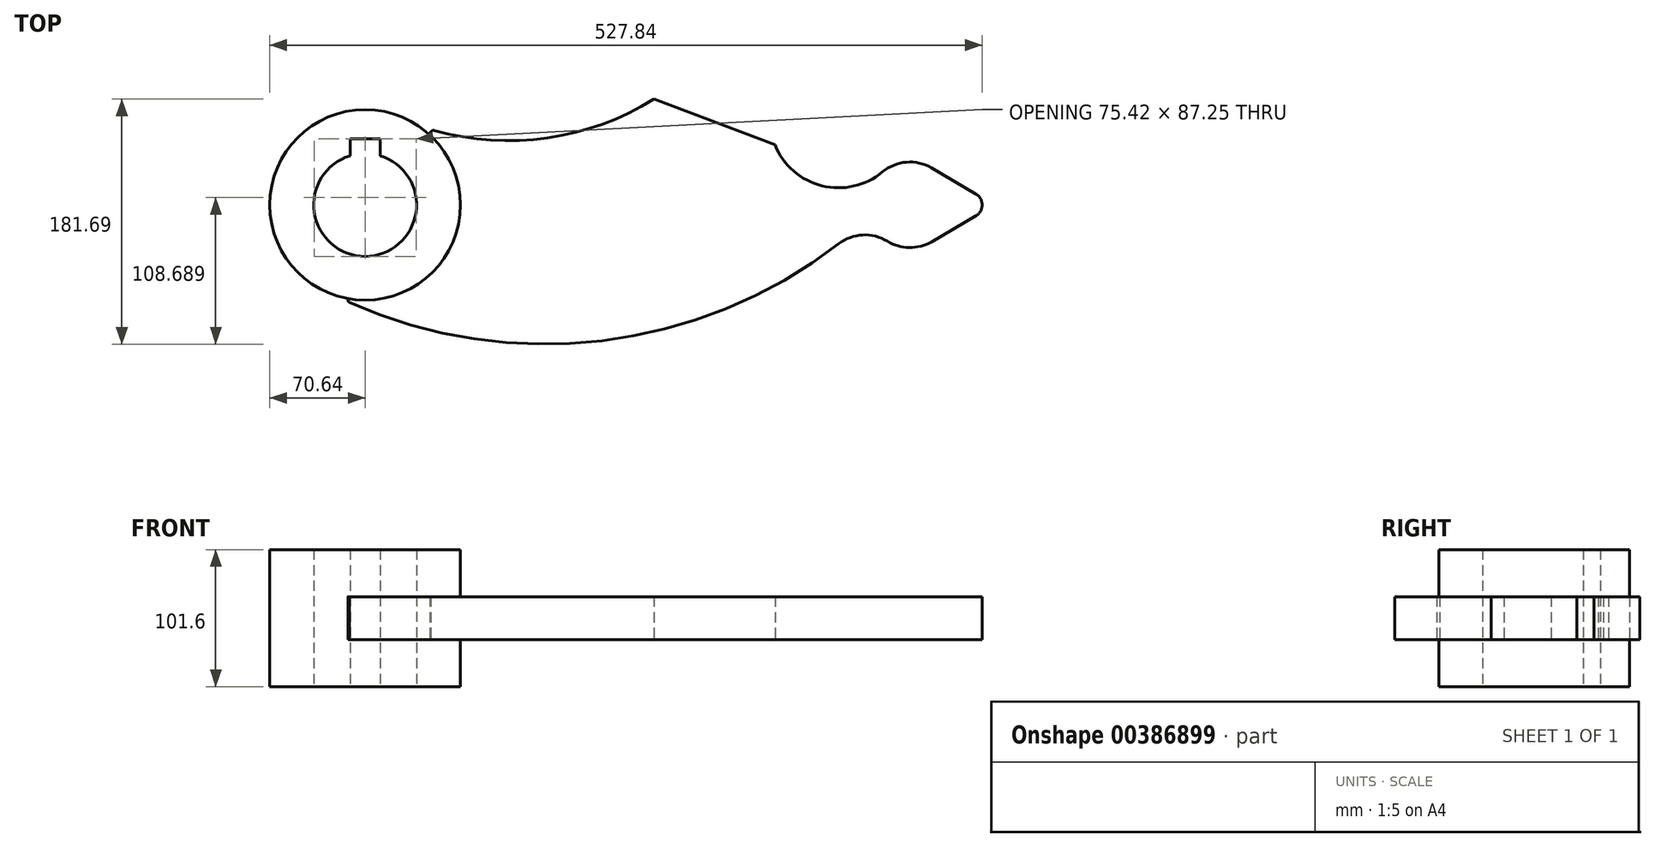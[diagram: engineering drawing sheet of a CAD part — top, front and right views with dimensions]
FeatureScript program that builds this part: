
annotation { "Feature Type Name" : "Feature", "Feature Type Description" : "" }
export const myFeature = defineFeature(function(context is Context, id is Id, definition is map)
    precondition{}
    {
        {
            var Q0;
            Q0=qCreatedBy(makeId("Top.planeOp"),FACE);
            var sketch = newSketch(context, id + "F0", { "sketchPlane" : qUnion([Q0])});
            skArc(sketch, "E0", {"start": v(51.32, 55.22) * mm, "mid": v(135.14, 49.67) * mm, "end": v(214.04, 78.5) * mm});
            skArc(sketch, "E1", {"start": v(303.74, 44.45) * mm, "mid": v(338.47, 14.23) * mm, "end": v(383.35, 24.47) * mm});
            skArc(sketch, "E2", {"start": v(452.47, -8.23) * mm, "mid": v(457.2, -0.02) * mm, "end": v(452.5, 8.21) * mm});
            skArc(sketch, "E3", {"start": v(387, -26.95) * mm, "mid": v(403.28, -31.67) * mm, "end": v(419.67, -27.35) * mm});
            skArc(sketch, "E4", {"start": v(387, -26.95) * mm, "mid": v(368.67, -22.27) * mm, "end": v(350.92, -28.86) * mm});
            skPoint(sketch, "E4.first.point", {"position": v(350.92, -28.86) * mm});
            skPoint(sketch, "E4.third.point", {"position": v(372.44, -85.66) * mm});
            skLineSegment(sketch, "E5", {"start": v(214.04, 78.5) * mm, "end": v(303.74, 44.45) * mm});
            skLineSegment(sketch, "E6", {"start": v(419.67, -27.35) * mm, "end": v(452.47, -8.23) * mm});
            skLineSegment(sketch, "E7", {"start": v(452.5, 8.21) * mm, "end": v(419.76, 27.45) * mm});
            skArc(sketch, "E8.trimOffspring", {"start": v(419.76, 27.45) * mm, "mid": v(401.08, 31.72) * mm, "end": v(383.35, 24.47) * mm});
            skArc(sketch, "E9", {"start": v(-11.14, -69.76) * mm, "mid": v(-12.63, -70.64) * mm, "end": v(-11.86, -72.19) * mm});
            skPoint(sketch, "E9.first.point", {"position": v(-11.14, -69.76) * mm});
            skPoint(sketch, "E9.second.point", {"position": v(-11.86, -72.19) * mm});
            skPoint(sketch, "E9.third.point", {"position": v(-12.67, -70.86) * mm});
            skArc(sketch, "E10", {"start": v(51.32, 55.22) * mm, "mid": v(48.32, 53.83) * mm, "end": v(49.24, 50.65) * mm});
            skPoint(sketch, "E10.first.point", {"position": v(49.24, 50.65) * mm});
            skPoint(sketch, "E10.second.point", {"position": v(51.32, 55.22) * mm});
            skPoint(sketch, "E10.third.point", {"position": v(52.69, 51.28) * mm});
            skArc(sketch, "E11.trimOffspring", {"start": v(-11.86, -72.19) * mm, "mid": v(175.52, -100.68) * mm, "end": v(350.92, -28.86) * mm});
            skArc(sketch, "E12.trimOffspring", {"start": v(-11.14, -69.76) * mm, "mid": v(63.15, -31.67) * mm, "end": v(49.24, 50.65) * mm});
            skSolve(sketch);
        }
        {
            var Q0;
            Q0 = qSketchRegion(id + "F0", true);
            extrude(context, id + "F1", {"entities" : qUnion([Q0]), "depth" : 31.75 * mm, "offsetDistance" : 25.4 * mm, "symmetric" : true});
        }
        {
            var Q0;
            Q0=qCreatedBy(makeId("Top.planeOp"),FACE);
            var sketch = newSketch(context, id + "F2", { "sketchPlane" : qUnion([Q0])});
            skCircle(sketch, "E13", {"center": v(0, 0) * mm, "radius": 70.64 * mm});
            skArc(sketch, "E14", {"start": v(-11.11, 36.47) * mm, "mid": v(0, -38.13) * mm, "end": v(11.11, 36.47) * mm});
            skLineSegment(sketch, "E15.bottom", {"start": v(11.11, 49.12) * mm, "end": v(-11.11, 49.12) * mm});
            skLineSegment(sketch, "E15.left", {"start": v(11.11, 49.12) * mm, "end": v(11.11, 36.47) * mm});
            skLineSegment(sketch, "E15.right", {"start": v(-11.11, 49.12) * mm, "end": v(-11.11, 36.47) * mm});
            skPoint(sketch, "E15.middle", {"position": v(0, 32.09) * mm});
            skPoint(sketch, "E15.top.end.orphan", {"position": v(-11.11, 15.05) * mm});
            skPoint(sketch, "E15.top.start.orphan", {"position": v(11.11, 15.05) * mm});
            skSolve(sketch);
        }
        {
            var Q0;
            Q0=makeQuery(id+"F2.imprint","IMPRINT",FACE,{"disambiguationData":[TD([[makeQuery(id+"F2.imprint","IMPRINT",EDGE,{"derivedFrom":sQuery(id+"F2.wireOp",EDGE,"E13")}),1.0]])]});
            extrude(context, id + "F3", {"entities" : qUnion([Q0]), "operationType" : NewBodyOperationType.ADD, "depth" : 101.6 * mm, "offsetDistance" : 25.4 * mm, "symmetric" : true});
        }
    });
